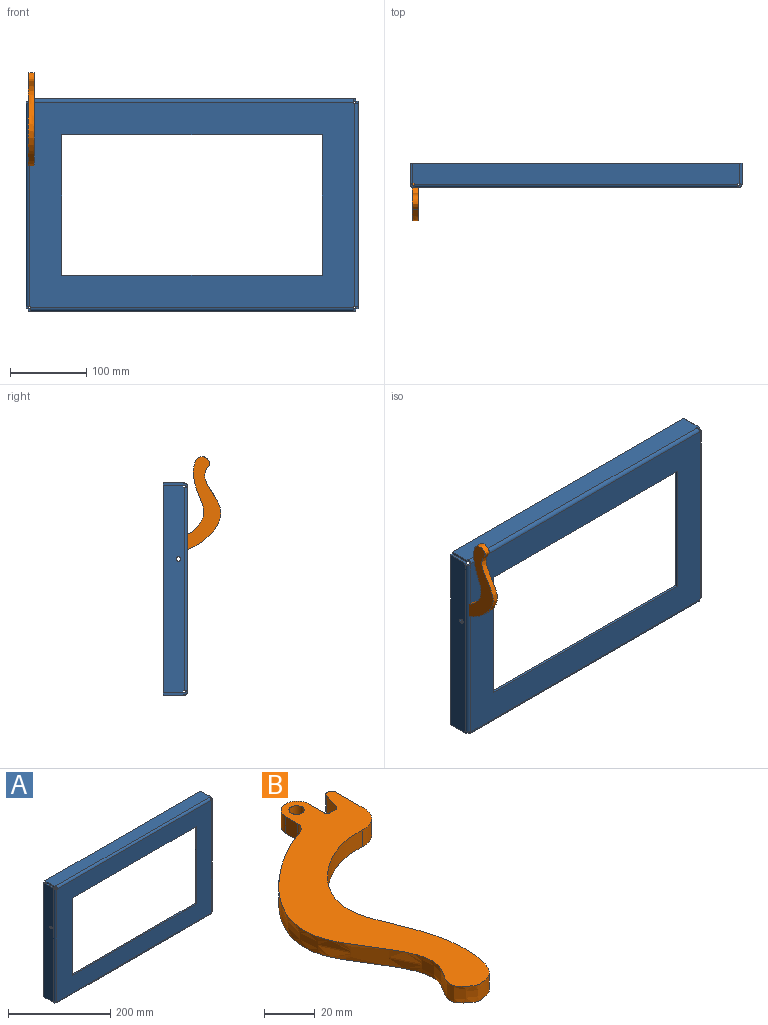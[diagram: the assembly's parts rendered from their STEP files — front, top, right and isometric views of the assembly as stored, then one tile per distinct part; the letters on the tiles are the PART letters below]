
ASSEMBLY  parts=2 mates=1
PART A: 68 faces, bbox 436x32x279 mm
  f0: plane 429.96x27.5mm, normal (0,0,-1), area 11817.9mm2, adj f1,f2,f4,f5,f6,f7,f8,f67
  f1: plane 26.35x3mm, normal (1,0,0), area 79.1mm2, adj f0,f3,f4,f6
  f2: plane 26.35x3mm, normal (-1,0,0), area 79.1mm2, adj f0,f3,f4,f8
  f3: plane 429.96x27.5mm, normal (0,0,1), area 11817.9mm2, adj f1,f2,f4,f5,f6,f7,f8,f66
  f4: plane 429.96x3mm, normal (0,1,0), area 1289.9mm2, adj f0,f1,f2,f3
  f5: plane 3x1.15mm, normal (1,0,0), area 3.4mm2, adj f0,f3,f6,f65
  f6: plane 3x2.61mm, normal (0,-1,0), area 7.8mm2, adj f0,f1,f3,f5
  f7: plane 3x1.15mm, normal (-1,0,0), area 3.4mm2, adj f0,f3,f8,f64
  f8: plane 3x2.61mm, normal (0,-1,0), area 7.8mm2, adj f0,f2,f3,f7
  f9: plane 427x270mm, normal (0,-1,0), area 52014.9mm2, adj f10,f11,f12,f13,f15,f16,f17,f18
  f10: plane 185x3mm, normal (-1,0,0), area 555mm2, adj f9,f11,f13,f14
  f11: plane 342x3mm, normal (0,0,1), area 1026mm2, adj f9,f10,f12,f14
  f12: plane 185x3mm, normal (1,0,0), area 555mm2, adj f9,f11,f13,f14
  f13: plane 342x3mm, normal (0,0,-1), area 1026mm2, adj f9,f10,f12,f14
  f14: plane 427x270mm, normal (0,1,0), area 52014.9mm2, adj f10,f11,f12,f13,f15,f16,f17,f18
  f15: plane 3x1.13mm, normal (1,0,0), area 3.4mm2, adj f9,f14,f16,f65
  f16: plane 3x1.13mm, normal (0,0,1), area 3.4mm2, adj f9,f14,f15,f47
  f17: plane 3x1.13mm, normal (0,0,1), area 3.4mm2, adj f9,f14,f18,f61
  f18: plane 3x1.13mm, normal (-1,0,0), area 3.4mm2, adj f9,f14,f17,f64
  f19: plane 3x1.13mm, normal (-1,0,0), area 3.4mm2, adj f9,f14,f20,f32
  f20: plane 3x1.13mm, normal (0,0,-1), area 3.4mm2, adj f9,f14,f19,f60
  f21: plane 3x1.13mm, normal (0,0,-1), area 3.4mm2, adj f9,f14,f22,f46
  f22: plane 3x1.13mm, normal (1,0,0), area 3.4mm2, adj f9,f14,f21,f33
  f23: plane 26.35x3mm, normal (-1,0,0), area 79.1mm2, adj f25,f26,f27,f29
  f24: plane 26.35x3mm, normal (1,0,0), area 79.1mm2, adj f25,f26,f27,f31
  f25: plane 429.96x27.5mm, normal (0,0,-1), area 11817.9mm2, adj f23,f24,f26,f28,f29,f30,f31,f34
  f26: plane 429.96x3mm, normal (0,1,0), area 1289.9mm2, adj f23,f24,f25,f27
  f27: plane 429.96x27.5mm, normal (0,0,1), area 11817.9mm2, adj f23,f24,f26,f28,f29,f30,f31,f35
  f28: plane 3x1.15mm, normal (-1,0,0), area 3.4mm2, adj f25,f27,f29,f32
  f29: plane 3x2.61mm, normal (0,-1,0), area 7.8mm2, adj f23,f25,f27,f28
  f30: plane 3x1.15mm, normal (1,0,0), area 3.4mm2, adj f25,f27,f31,f33
  f31: plane 3x2.61mm, normal (0,-1,0), area 7.8mm2, adj f24,f25,f27,f30
  f32: plane 4.5x4.5mm, normal (-1,0,0), area 14.1mm2, adj f19,f28,f34,f35
  f33: plane 4.5x4.5mm, normal (1,0,0), area 14.1mm2, adj f22,f30,f34,f35
  f34: cylinder r=4.5mm len=424.75mm, axis (-1,0,0), area 3002.4mm2, adj f9,f25,f32,f33
  f35: cylinder r=1.5mm len=424.75mm, axis (-1,0,0), area 1000.8mm2, adj f14,f27,f32,f33
  f36: plane 26.35x3mm, normal (0,0,-1), area 79.1mm2, adj f38,f39,f41,f43
  f37: plane 26.35x3mm, normal (0,0,1), area 79.1mm2, adj f38,f39,f41,f45
  f38: plane 272.96x27.5mm, normal (1,0,0), area 7472.1mm2, adj f36,f37,f39,f40,f42,f43,f44,f45
  f39: plane 272.96x3mm, normal (0,1,0), area 818.9mm2, adj f36,f37,f38,f41
  f40: cylinder r=3mm len=6mm, axis (1,0,0), area 56.5mm2, adj f38,f41
  f41: plane 272.96x27.5mm, normal (-1,0,0), area 7472.1mm2, adj f36,f37,f39,f40,f42,f43,f44,f45
  f42: plane 3x1.15mm, normal (0,0,-1), area 3.4mm2, adj f38,f41,f43,f46
  f43: plane 3x2.61mm, normal (0,-1,0), area 7.8mm2, adj f36,f38,f41,f42
  f44: plane 3x1.15mm, normal (0,0,1), area 3.4mm2, adj f38,f41,f45,f47
  f45: plane 3x2.61mm, normal (0,-1,0), area 7.8mm2, adj f37,f38,f41,f44
  f46: plane 4.5x4.5mm, normal (0,0,-1), area 14.1mm2, adj f21,f42,f48,f49
  f47: plane 4.5x4.5mm, normal (0,0,1), area 14.1mm2, adj f16,f44,f48,f49
  f48: cylinder r=4.5mm len=267.75mm, axis (0,0,-1), area 1892.6mm2, adj f9,f38,f46,f47
  f49: cylinder r=1.5mm len=267.75mm, axis (0,0,-1), area 630.9mm2, adj f14,f41,f46,f47
  f50: plane 272.96x27.5mm, normal (1,0,0), area 7472.1mm2, adj f51,f52,f54,f55,f56,f57,f58,f59
  f51: plane 26.35x3mm, normal (0,0,1), area 79.1mm2, adj f50,f53,f54,f57
  f52: plane 26.35x3mm, normal (0,0,-1), area 79.1mm2, adj f50,f53,f54,f59
  f53: plane 272.96x27.5mm, normal (-1,0,0), area 7472.1mm2, adj f51,f52,f54,f55,f56,f57,f58,f59
  f54: plane 272.96x3mm, normal (0,1,0), area 818.9mm2, adj f50,f51,f52,f53
  f55: cylinder r=3mm len=6mm, axis (1,0,0), area 56.5mm2, adj f50,f53
  f56: plane 3x1.15mm, normal (0,0,1), area 3.4mm2, adj f50,f53,f57,f61
  f57: plane 3x2.61mm, normal (0,-1,0), area 7.8mm2, adj f50,f51,f53,f56
  f58: plane 3x1.15mm, normal (0,0,-1), area 3.4mm2, adj f50,f53,f59,f60
  f59: plane 3x2.61mm, normal (0,-1,0), area 7.8mm2, adj f50,f52,f53,f58
  f60: plane 4.5x4.5mm, normal (0,0,-1), area 14.1mm2, adj f20,f58,f62,f63
  f61: plane 4.5x4.5mm, normal (0,0,1), area 14.1mm2, adj f17,f56,f62,f63
  f62: cylinder r=4.5mm len=267.75mm, axis (0,0,-1), area 1892.6mm2, adj f9,f53,f60,f61
  f63: cylinder r=1.5mm len=267.75mm, axis (0,0,-1), area 630.9mm2, adj f14,f50,f60,f61
  f64: plane 4.5x4.5mm, normal (-1,0,0), area 14.1mm2, adj f7,f18,f66,f67
  f65: plane 4.5x4.5mm, normal (1,0,0), area 14.1mm2, adj f5,f15,f66,f67
  f66: cylinder r=4.5mm len=424.75mm, axis (-1,0,0), area 3002.4mm2, adj f3,f9,f64,f65
  f67: cylinder r=1.5mm len=424.75mm, axis (-1,0,0), area 1000.8mm2, adj f0,f14,f64,f65
PART B: 19 faces, bbox 78.5x140.3x8 mm
  f0: plane 140.33x78.5mm, normal (0,0,1), area 3156.4mm2, adj f2,f3,f4,f5,f6,f7,f8,f9
  f1: plane 140.33x78.5mm, normal (0,0,-1), area 3156.4mm2, adj f2,f3,f4,f5,f6,f7,f8,f9
  f2: extruded ~122.87x63.96mm, area 2373.7mm2, adj f0,f1,f3,f17
  f3: cylinder r=10mm len=10.74mm, axis (0,0,-1), area 131.6mm2, adj f0,f1,f2,f4
  f4: plane 15.94x8mm, normal (1,0,0), area 127.5mm2, adj f0,f1,f3,f5
  f5: cylinder r=2mm len=8mm, axis (0,0,-1), area 25.1mm2, adj f0,f1,f4,f6
  f6: plane 8x0.52mm, normal (0,1,0), area 4.2mm2, adj f0,f1,f5,f7
  f7: cylinder r=2mm len=8mm, axis (0,0,-1), area 20.4mm2, adj f0,f1,f6,f8
  f8: plane 8x7.77mm, normal (-0.96,0.29,0), area 65mm2, adj f0,f1,f7,f9
  f9: cylinder r=2mm len=8mm, axis (0,0,-1), area 20.4mm2, adj f0,f1,f8,f10
  f10: plane 8x2.52mm, normal (0,1,0), area 20.2mm2, adj f0,f1,f9,f11
  f11: cylinder r=2mm len=8mm, axis (0,0,-1), area 25.1mm2, adj f0,f1,f10,f12
  f12: plane 8.5x8mm, normal (1,0,0), area 68mm2, adj f0,f1,f11,f13
  f13: cylinder r=6mm len=8mm, axis (0,0,-1), area 75.4mm2, adj f0,f1,f12,f14
  f14: plane 8x0.5mm, normal (0,1,0), area 4mm2, adj f0,f1,f13,f15
  f15: cylinder r=6mm len=8mm, axis (0,0,-1), area 75.4mm2, adj f0,f1,f14,f16
  f16: plane 8x6.66mm, normal (-1,0,0), area 53.3mm2, adj f0,f1,f15,f17
  f17: cylinder r=5mm len=8mm, axis (0,0,-1), area 50.7mm2, adj f0,f1,f2,f16
  f18: cylinder r=3mm len=8mm, axis (0,0,-1), area 150.8mm2, adj f0,f1
PLACE A t=(-137.36,-16.39,-15.66)mm
PLACE B rot(axis=(-0.58,-0.58,0.58),120deg) t=(-344.36,-54.37,48.99)mm
MATE fastened B.f15 <-> A.f40  axis (-1,0,0) through (-352.36,-36.39,23.84)mm
